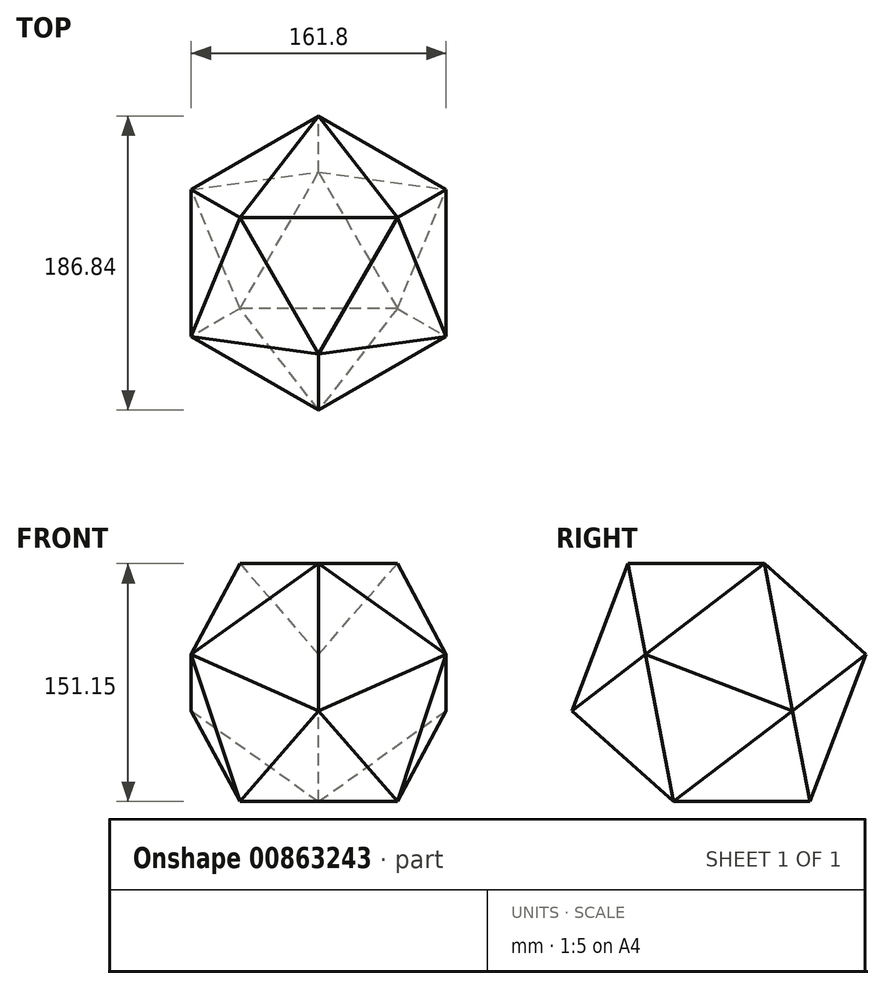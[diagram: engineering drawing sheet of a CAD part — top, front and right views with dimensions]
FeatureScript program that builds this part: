
annotation { "Feature Type Name" : "Feature", "Feature Type Description" : "" }
export const myFeature = defineFeature(function(context is Context, id is Id, definition is map)
    precondition{}
    {
        {
            var Q0;
            Q0=qCreatedBy(makeId("Top.planeOp"),FACE);
            var sketch = newSketch(context, id + "F0", { "sketchPlane" : qUnion([Q0])});
            skCircle(sketch, "E0.cCircle", {"center": v(0, 0) * mm, "radius": 28.87 * mm, "construction": true});
            skLineSegment(sketch, "E0.0", {"start": v(-50, -28.87) * mm, "end": v(0, 57.74) * mm});
            skLineSegment(sketch, "E0.1", {"start": v(0, 57.74) * mm, "end": v(50, -28.87) * mm});
            skLineSegment(sketch, "E0.2", {"start": v(50, -28.87) * mm, "end": v(-50, -28.87) * mm});
            skPoint(sketch, "E0.0.midPoint", {"position": v(-25, 14.43) * mm});
            skLineSegment(sketch, "E1", {"start": v(-25, 14.43) * mm, "end": v(50, -28.87) * mm, "construction": true});
            skSolve(sketch);
        }
        {
            var Q0;
            Q0=qCreatedBy(makeId("Front.planeOp"),FACE);
            var sketch = newSketch(context, id + "F1", { "sketchPlane" : qUnion([Q0])});
            skLineSegment(sketch, "E2", {"start": v(0, 0) * mm, "end": v(0, 75.58) * mm});
            skSolve(sketch);
        }
        {
            var Q0;
            Q0=makeQuery(id+"F0.imprint","IMPRINT",FACE,{"disambiguationData":[TD([[makeQuery(id+"F0.imprint","IMPRINT",EDGE,{"derivedFrom":sQuery(id+"F0.wireOp",EDGE,"E0.0")}),-1.0]])]});
            var Q1;
            Q1=sQuery(id+"F1.wireOp",VERTEX,"E2.end");
            loft(context, id + "F2", {"sheetProfilesArray" : [{ "sheetProfileEntities" : qUnion([Q0]) }, { "sheetProfileEntities" : qUnion([Q1]) }]});
        }
        {
            var Q0;
            Q0=makeQuery(id+"F2.opLoft","SWEPT_BODY",BODY,{"disambiguationData":[OSD([makeQuery(id+"F0.imprint","IMPRINT",FACE,{"disambiguationData":[TD([[makeQuery(id+"F0.imprint","IMPRINT",EDGE,{"derivedFrom":sQuery(id+"F0.wireOp",EDGE,"E0.0")}),-1.0]])]}),sQuery(id+"F1.wireOp",VERTEX,"E2.end")])]});
            var Q1;
            Q1=makeQuery(id+"F2.opLoft","SWEPT_EDGE",EDGE,{"disambiguationData":[OSD([sQuery(id+"F0.wireOp",EDGE,"E0.1"),sQuery(id+"F0.wireOp",EDGE,"E0.2"),sQuery(id+"F1.wireOp",VERTEX,"E2.end")])]});
            circularPattern(context, id + "F3", {"operationType" : NewBodyOperationType.ADD, "entities" : qUnion([Q0]), "axis" : qUnion([Q1]), "angle" : 360 * degree, "instanceCount" : 5, "equalSpace" : true});
        }
        {
            var Q0;
            Q0=makeQuery(id+"F2.opLoft","SWEPT_BODY",BODY,{"disambiguationData":[OSD([makeQuery(id+"F0.imprint","IMPRINT",FACE,{"disambiguationData":[TD([[makeQuery(id+"F0.imprint","IMPRINT",EDGE,{"derivedFrom":sQuery(id+"F0.wireOp",EDGE,"E0.0")}),-1.0]])]}),sQuery(id+"F1.wireOp",VERTEX,"E2.end")])]});
            var Q1;
            {var subQ0=sQuery(id+"F1.wireOp",VERTEX,"E2.end");var subQ1=sQuery(id+"F0.wireOp",EDGE,"E0.0");Q1=makeQuery(id+"F3.boolean.opBoolean","MERGE",EDGE,{"derivedFrom":[makeQuery(id+"F2.opLoft","SWEPT_EDGE",EDGE,{"disambiguationData":[OSD([subQ1,sQuery(id+"F0.wireOp",EDGE,"E0.2"),subQ0])]}),makeQuery(id+"F3.opPattern","COPY",EDGE,{"derivedFrom":makeQuery(id+"F2.opLoft","SWEPT_EDGE",EDGE,{"disambiguationData":[OSD([subQ1,sQuery(id+"F0.wireOp",EDGE,"E0.1"),subQ0])]}),"instanceName":"1"})]});}
            circularPattern(context, id + "F4", {"operationType" : NewBodyOperationType.ADD, "entities" : qUnion([Q0]), "axis" : qUnion([Q1]), "angle" : 360 * degree, "instanceCount" : 5, "equalSpace" : true});
        }
        {
            var Q0;
            Q0=makeQuery(id+"F2.opLoft","SWEPT_BODY",BODY,{"disambiguationData":[OSD([makeQuery(id+"F0.imprint","IMPRINT",FACE,{"disambiguationData":[TD([[makeQuery(id+"F0.imprint","IMPRINT",EDGE,{"derivedFrom":sQuery(id+"F0.wireOp",EDGE,"E0.0")}),-1.0]])]}),sQuery(id+"F1.wireOp",VERTEX,"E2.end")])]});
            var Q1;
            {var subQ0=sQuery(id+"F1.wireOp",VERTEX,"E2.end");var subQ1=sQuery(id+"F0.wireOp",EDGE,"E0.0");var subQ2=makeQuery(id+"F2.opLoft","SWEPT_EDGE",EDGE,{"disambiguationData":[OSD([subQ1,sQuery(id+"F0.wireOp",EDGE,"E0.1"),subQ0])]});var subQ3=makeQuery(id+"F2.opLoft","SWEPT_EDGE",EDGE,{"disambiguationData":[OSD([subQ1,sQuery(id+"F0.wireOp",EDGE,"E0.2"),subQ0])]});Q1=makeQuery(id+"F4.boolean.opBoolean","MERGE",EDGE,{"derivedFrom":[makeQuery(id+"F4.opPattern","COPY",EDGE,{"derivedFrom":makeQuery(id+"F3.boolean.opBoolean","MERGE",EDGE,{"derivedFrom":[makeQuery(id+"F3.opPattern","COPY",EDGE,{"derivedFrom":subQ3,"instanceName":"3"}),makeQuery(id+"F3.opPattern","COPY",EDGE,{"derivedFrom":subQ2,"instanceName":"4"})]}),"instanceName":"1"}),makeQuery(id+"F4.opPattern","COPY",EDGE,{"derivedFrom":makeQuery(id+"F3.boolean.opBoolean","MERGE",EDGE,{"derivedFrom":[makeQuery(id+"F3.opPattern","COPY",EDGE,{"derivedFrom":subQ3,"instanceName":"2"}),makeQuery(id+"F3.opPattern","COPY",EDGE,{"derivedFrom":subQ2,"instanceName":"3"})]}),"instanceName":"2"})]});}
            circularPattern(context, id + "F5", {"operationType" : NewBodyOperationType.ADD, "entities" : qUnion([Q0]), "axis" : qUnion([Q1]), "angle" : 360 * degree, "instanceCount" : 5, "equalSpace" : true});
        }
    });
